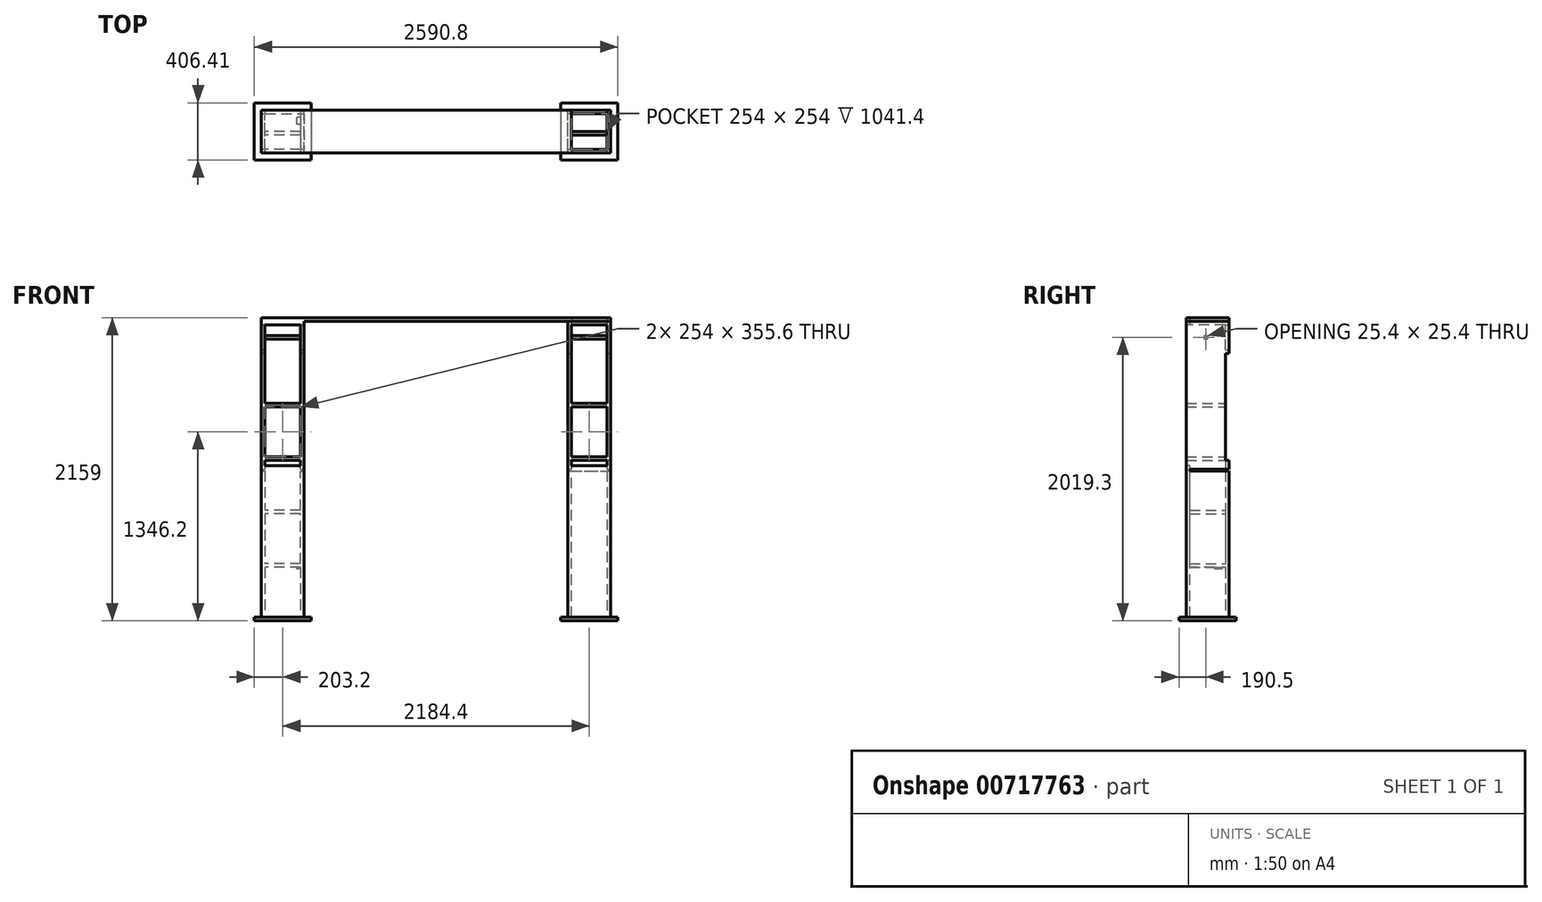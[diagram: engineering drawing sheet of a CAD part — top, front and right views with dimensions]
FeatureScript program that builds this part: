
annotation { "Feature Type Name" : "Feature", "Feature Type Description" : "" }
export const myFeature = defineFeature(function(context is Context, id is Id, definition is map)
    precondition{}
    {
        {
            var Q0;
            Q0=qCreatedBy(makeId("Front.planeOp"),FACE);
            var sketch = newSketch(context, id + "F0", { "sketchPlane" : qUnion([Q0])});
            skLineSegment(sketch, "E0", {"start": v(0, 0) * mm, "end": v(939.8, 0) * mm});
            skLineSegment(sketch, "E1", {"start": v(939.8, 0) * mm, "end": v(939.8, 1066.8) * mm});
            skLineSegment(sketch, "E2", {"start": v(939.8, 1066.8) * mm, "end": v(1244.6, 1066.8) * mm});
            skLineSegment(sketch, "E3", {"start": v(1244.6, 1066.8) * mm, "end": v(1244.6, 0) * mm});
            skLineSegment(sketch, "E4.MirrorCS", {"start": v(0, 0) * mm, "end": v(-939.8, 0) * mm});
            skLineSegment(sketch, "E5.MirrorCS", {"start": v(-939.8, 0) * mm, "end": v(-939.8, 1066.8) * mm});
            skLineSegment(sketch, "E6.MirrorCS", {"start": v(-939.8, 1066.8) * mm, "end": v(-1244.6, 1066.8) * mm});
            skLineSegment(sketch, "E7.MirrorCS", {"start": v(-1244.6, 1066.8) * mm, "end": v(-1244.6, 0) * mm});
            skLineSegment(sketch, "E8.MirrorCS", {"start": v(-939.8, 0) * mm, "end": v(-939.8, -1066.8) * mm});
            skLineSegment(sketch, "E9.MirrorCS", {"start": v(-1244.6, -1066.8) * mm, "end": v(-1244.6, 0) * mm});
            skLineSegment(sketch, "E10.MirrorCS", {"start": v(-939.8, -1066.8) * mm, "end": v(-1244.6, -1066.8) * mm});
            skLineSegment(sketch, "E11.MirrorCS", {"start": v(939.8, 0) * mm, "end": v(939.8, -1066.8) * mm});
            skLineSegment(sketch, "E12.MirrorCS", {"start": v(1244.6, -1066.8) * mm, "end": v(1244.6, 0) * mm});
            skLineSegment(sketch, "E13.MirrorCS", {"start": v(939.8, -1066.8) * mm, "end": v(1244.6, -1066.8) * mm});
            skLineSegment(sketch, "E14", {"start": v(939.8, 0) * mm, "end": v(1244.6, 0) * mm});
            skLineSegment(sketch, "E15", {"start": v(939.8, 0) * mm, "end": v(939.8, 12.7) * mm});
            skLineSegment(sketch, "E16", {"start": v(939.8, 12.7) * mm, "end": v(1244.6, 12.7) * mm});
            skLineSegment(sketch, "E17", {"start": v(1244.6, 12.7) * mm, "end": v(1244.6, 0) * mm});
            skLineSegment(sketch, "E18.MirrorCS", {"start": v(-939.8, 12.7) * mm, "end": v(-1244.6, 12.7) * mm});
            skLineSegment(sketch, "E19.MirrorCS", {"start": v(-939.8, 0) * mm, "end": v(-1244.6, 0) * mm});
            skLineSegment(sketch, "E20", {"start": v(-939.8, 12.7) * mm, "end": v(-939.8, 0) * mm});
            skLineSegment(sketch, "E21", {"start": v(-1244.6, 12.7) * mm, "end": v(-1244.6, 0) * mm});
            skSolve(sketch);
        }
        {
            var Q0;
            Q0=makeQuery(id+"F0.imprint","IMPRINT",FACE,{"disambiguationData":[TD([[makeQuery(id+"F0.imprint","IMPRINT",EDGE,{"derivedFrom":sQuery(id+"F0.wireOp",EDGE,"E1")}),-1.0]])]});
            var Q1;
            Q1=makeQuery(id+"F0.imprint","IMPRINT",FACE,{"disambiguationData":[TD([[makeQuery(id+"F0.imprint","IMPRINT",EDGE,{"derivedFrom":sQuery(id+"F0.wireOp",EDGE,"E11.MirrorCS")}),1.0]])]});
            var Q2;
            Q2=makeQuery(id+"F0.imprint","IMPRINT",FACE,{"disambiguationData":[TD([[makeQuery(id+"F0.imprint","IMPRINT",EDGE,{"derivedFrom":sQuery(id+"F0.wireOp",EDGE,"E5.MirrorCS")}),1.0]])]});
            var Q3;
            Q3=makeQuery(id+"F0.imprint","IMPRINT",FACE,{"disambiguationData":[TD([[makeQuery(id+"F0.imprint","IMPRINT",EDGE,{"derivedFrom":sQuery(id+"F0.wireOp",EDGE,"E8.MirrorCS")}),-1.0]])]});
            extrude(context, id + "F1", {"entities" : qUnion([Q0, Q1, Q2, Q3]), "depth" : 25.4 * mm, "offsetDistance" : 25.4 * mm});
        }
        {
            var Q0;
            Q0=makeQuery(id+"F1.opExtrude","SWEPT_FACE",FACE,{"disambiguationData":[OSD([sQuery(id+"F0.wireOp",EDGE,"E3"),sQuery(id+"F0.wireOp",EDGE,"E12.MirrorCS")])]});
            var sketch = newSketch(context, id + "F2", { "sketchPlane" : qUnion([Q0])});
            skLineSegment(sketch, "E22", {"start": v(0, 1066.8) * mm, "end": v(279.4, 1066.8) * mm});
            skLineSegment(sketch, "E23", {"start": v(0, -1066.8) * mm, "end": v(279.4, -1066.8) * mm});
            skLineSegment(sketch, "E24", {"start": v(279.4, 1066.8) * mm, "end": v(279.4, -1066.8) * mm});
            skLineSegment(sketch, "E25", {"start": v(0, 12.7) * mm, "end": v(279.4, 12.7) * mm});
            skLineSegment(sketch, "E26", {"start": v(0, 0) * mm, "end": v(279.4, 0) * mm});
            skLineSegment(sketch, "E27", {"start": v(279.4, 0) * mm, "end": v(279.4, 12.7) * mm});
            skLineSegment(sketch, "E28", {"start": v(0, 12.7) * mm, "end": v(0, 0) * mm});
            skLineSegment(sketch, "E29", {"start": v(0, 1066.8) * mm, "end": v(2.54, 1066.8) * mm});
            skLineSegment(sketch, "E30", {"start": v(2.54, 1066.8) * mm, "end": v(2.54, -1066.8) * mm});
            skPoint(sketch, "E30.endSnap0", {"position": v(139.7, -1066.8) * mm});
            skLineSegment(sketch, "E31", {"start": v(2.54, -1066.8) * mm, "end": v(0, -1066.8) * mm});
            skSolve(sketch);
        }
        {
            var Q0;
            {var subQ0=sQuery(id+"F2.wireOp",EDGE,"E22");Q0=makeQuery(id+"F2.imprint","IMPRINT",FACE,{"disambiguationData":[TD([[makeQuery(id+"F2.imprint","IMPRINT",EDGE,{"derivedFrom":subQ0}),-1.0]])]});}
            var Q1;
            {var subQ0=sQuery(id+"F2.wireOp",EDGE,"E23");Q1=makeQuery(id+"F2.imprint","IMPRINT",FACE,{"disambiguationData":[TD([[makeQuery(id+"F2.imprint","IMPRINT",EDGE,{"derivedFrom":subQ0}),1.0]])]});}
            extrude(context, id + "F3", {"entities" : qUnion([Q0, Q1]), "oppositeDirection" : true, "depth" : 25.4 * mm, "offsetDistance" : 25.4 * mm});
        }
        {
            var Q0;
            Q0=makeQuery(id+"F3.opExtrude","SWEPT_FACE",FACE,{"disambiguationData":[OSD([sQuery(id+"F2.wireOp",EDGE,"E24")])]});
            var sketch = newSketch(context, id + "F4", { "sketchPlane" : qUnion([Q0])});
            skLineSegment(sketch, "E32", {"start": v(-1219.2, 1066.8) * mm, "end": v(-965.2, 1066.8) * mm});
            skLineSegment(sketch, "E33", {"start": v(-1219.2, -1066.8) * mm, "end": v(-965.2, -1066.8) * mm});
            skLineSegment(sketch, "E34", {"start": v(-965.2, 1066.8) * mm, "end": v(-965.2, -1066.8) * mm});
            skLineSegment(sketch, "E35", {"start": v(-1219.2, 12.7) * mm, "end": v(-965.2, 12.7) * mm});
            skLineSegment(sketch, "E36", {"start": v(-965.2, 12.7) * mm, "end": v(-965.2, 0) * mm});
            skLineSegment(sketch, "E37", {"start": v(-965.2, 0) * mm, "end": v(-1219.2, 0) * mm});
            skLineSegment(sketch, "E38", {"start": v(-1219.2, 0) * mm, "end": v(-1219.2, 12.7) * mm});
            skSolve(sketch);
        }
        {
            var Q0;
            {var subQ0=sQuery(id+"F4.wireOp",EDGE,"E33");Q0=makeQuery(id+"F4.imprint","IMPRINT",FACE,{"disambiguationData":[TD([[makeQuery(id+"F4.imprint","IMPRINT",EDGE,{"derivedFrom":subQ0}),1.0]])]});}
            var Q1;
            {var subQ0=sQuery(id+"F4.wireOp",EDGE,"E32");Q1=makeQuery(id+"F4.imprint","IMPRINT",FACE,{"disambiguationData":[TD([[makeQuery(id+"F4.imprint","IMPRINT",EDGE,{"derivedFrom":subQ0}),-1.0]])]});}
            extrude(context, id + "F5", {"entities" : qUnion([Q0, Q1]), "oppositeDirection" : true, "depth" : 25.4 * mm, "offsetDistance" : 25.4 * mm});
        }
        {
            var Q0;
            Q0=makeQuery(id+"F5.opExtrude","SWEPT_FACE",FACE,{"disambiguationData":[OSD([sQuery(id+"F4.wireOp",EDGE,"E34")])]});
            var sketch = newSketch(context, id + "F6", { "sketchPlane" : qUnion([Q0])});
            skLineSegment(sketch, "E39", {"start": v(-279.4, 1066.8) * mm, "end": v(0, 1066.8) * mm});
            skLineSegment(sketch, "E40", {"start": v(-279.4, -1066.8) * mm, "end": v(0, -1066.8) * mm});
            skLineSegment(sketch, "E41", {"start": v(0, -1066.8) * mm, "end": v(0, 1066.8) * mm});
            skLineSegment(sketch, "E42", {"start": v(-279.4, 1066.8) * mm, "end": v(-279.4, -1066.8) * mm});
            skLineSegment(sketch, "E43", {"start": v(0, 0) * mm, "end": v(0, 12.7) * mm});
            skLineSegment(sketch, "E44", {"start": v(0, 12.7) * mm, "end": v(-279.4, 12.7) * mm});
            skLineSegment(sketch, "E45", {"start": v(-279.4, 12.7) * mm, "end": v(-279.4, 0) * mm});
            skLineSegment(sketch, "E46", {"start": v(-279.4, 0) * mm, "end": v(0, 0) * mm});
            skSolve(sketch);
        }
        {
            var Q0;
            {var subQ2=sQuery(id+"F6.wireOp",EDGE,"E41");Q0=makeQuery(id+"F6.imprint","IMPRINT",FACE,{"disambiguationData":[TD([[makeQuery(id+"F6.imprint","IMPRINT",EDGE,{"derivedFrom":subQ2}),1.0]])]});}
            var Q1;
            {var subQ0=sQuery(id+"F6.wireOp",EDGE,"E42");Q1=makeQuery(id+"F6.imprint","IMPRINT",FACE,{"disambiguationData":[TD([[makeQuery(id+"F6.imprint","IMPRINT",EDGE,{"derivedFrom":subQ0}),1.0]])]});}
            extrude(context, id + "F7", {"entities" : qUnion([Q0, Q1]), "depth" : 25.4 * mm, "offsetDistance" : 25.4 * mm});
        }
        {
            var Q0;
            Q0=makeQuery(id+"F5.opExtrude","SWEPT_BODY",BODY,{"disambiguationData":[OSD([sQuery(id+"F2.wireOp",EDGE,"E24"),sQuery(id+"F4.wireOp",EDGE,"E32"),sQuery(id+"F4.wireOp",EDGE,"E33"),sQuery(id+"F4.wireOp",EDGE,"E34")])]});
            var Q1;
            Q1=makeQuery(id+"F7.opExtrude","SWEPT_BODY",BODY,{"disambiguationData":[OSD([sQuery(id+"F6.wireOp",EDGE,"E39"),sQuery(id+"F6.wireOp",EDGE,"E40"),sQuery(id+"F6.wireOp",EDGE,"E41"),sQuery(id+"F6.wireOp",EDGE,"E42")])]});
            var Q2;
            Q2=makeQuery(id+"F1.opExtrude","SWEPT_BODY",BODY,{"disambiguationData":[OSD([sQuery(id+"F0.wireOp",EDGE,"E1"),sQuery(id+"F0.wireOp",EDGE,"E2"),sQuery(id+"F0.wireOp",EDGE,"E3"),sQuery(id+"F0.wireOp",EDGE,"E11.MirrorCS"),sQuery(id+"F0.wireOp",EDGE,"E12.MirrorCS"),sQuery(id+"F0.wireOp",EDGE,"E13.MirrorCS")])]});
            var Q3;
            Q3=makeQuery(id+"F3.opExtrude","SWEPT_BODY",BODY,{"disambiguationData":[OSD([sQuery(id+"F0.wireOp",EDGE,"E3"),sQuery(id+"F0.wireOp",EDGE,"E12.MirrorCS"),sQuery(id+"F2.wireOp",EDGE,"E22"),sQuery(id+"F2.wireOp",EDGE,"E23"),sQuery(id+"F2.wireOp",EDGE,"E24")])]});
            var Q4;
            Q4=qCreatedBy(makeId("Right.planeOp"),FACE);
            mirror(context, id + "F8", {"operationType" : NewBodyOperationType.ADD, "entities" : qUnion([Q0, Q1, Q2, Q3]), "mirrorPlane" : qUnion([Q4])});
        }
        {
            var Q0;
            Q0=makeQuery(id+"F8.boolean.opBoolean","MERGE",FACE,{"derivedFrom":[makeQuery(id+"F1.opExtrude","SWEPT_FACE",FACE,{"disambiguationData":[OSD([sQuery(id+"F0.wireOp",EDGE,"E13.MirrorCS")])]}),makeQuery(id+"F3.opExtrude","SWEPT_FACE",FACE,{"disambiguationData":[OSD([sQuery(id+"F2.wireOp",EDGE,"E23")])]}),makeQuery(id+"F5.opExtrude","SWEPT_FACE",FACE,{"disambiguationData":[OSD([sQuery(id+"F4.wireOp",EDGE,"E33")])]}),makeQuery(id+"F7.opExtrude","SWEPT_FACE",FACE,{"disambiguationData":[OSD([sQuery(id+"F6.wireOp",EDGE,"E40")])]})]});
            var sketch = newSketch(context, id + "F9", { "sketchPlane" : qUnion([Q0])});
            skLineSegment(sketch, "E47", {"start": v(939.8, 25.4) * mm, "end": v(889, 25.4) * mm});
            skLineSegment(sketch, "E48", {"start": v(939.8, 25.4) * mm, "end": v(939.8, 76.2) * mm});
            skLineSegment(sketch, "E49", {"start": v(1244.6, -279.4) * mm, "end": v(1295.4, -279.4) * mm});
            skLineSegment(sketch, "E50", {"start": v(1244.6, -279.4) * mm, "end": v(1244.6, -330.2) * mm});
            skLineSegment(sketch, "E51", {"start": v(1295.4, -279.4) * mm, "end": v(1295.4, -330.2) * mm});
            skLineSegment(sketch, "E52", {"start": v(1295.4, -330.2) * mm, "end": v(1244.6, -330.2) * mm});
            skLineSegment(sketch, "E53", {"start": v(889, 25.4) * mm, "end": v(889, 76.2) * mm});
            skLineSegment(sketch, "E54", {"start": v(889, 76.2) * mm, "end": v(939.8, 76.2) * mm});
            skLineSegment(sketch, "E55", {"start": v(939.8, 76.2) * mm, "end": v(1295.4, 76.2) * mm});
            skLineSegment(sketch, "E56", {"start": v(1295.4, 76.2) * mm, "end": v(1295.4, -279.4) * mm});
            skLineSegment(sketch, "E57", {"start": v(1244.6, -330.2) * mm, "end": v(889, -330.2) * mm});
            skLineSegment(sketch, "E58", {"start": v(889, -330.2) * mm, "end": v(889, 25.4) * mm});
            skSolve(sketch);
        }
        {
            var Q0;
            Q0=makeQuery(id+"F9.imprint","IMPRINT",FACE,{"disambiguationData":[TD([[makeQuery(id+"F9.imprint","IMPRINT",EDGE,{"derivedFrom":sQuery(id+"F9.wireOp",EDGE,"E47")}),1.0]])]});
            var Q1;
            Q1=makeQuery(id+"F9.imprint","IMPRINT",FACE,{"disambiguationData":[TD([[makeQuery(id+"F9.imprint","IMPRINT",EDGE,{"derivedFrom":sQuery(id+"F9.wireOp",EDGE,"E47")}),-1.0]])]});
            var Q2;
            Q2=makeQuery(id+"F9.imprint","IMPRINT",FACE,{"disambiguationData":[TD([[makeQuery(id+"F9.imprint","IMPRINT",EDGE,{"derivedFrom":sQuery(id+"F9.wireOp",EDGE,"E48")}),-1.0]])]});
            var Q3;
            Q3=makeQuery(id+"F9.imprint","IMPRINT",FACE,{"disambiguationData":[TD([[makeQuery(id+"F9.imprint","IMPRINT",EDGE,{"derivedFrom":sQuery(id+"F9.wireOp",EDGE,"E49")}),-1.0]])]});
            extrude(context, id + "F10", {"entities" : qUnion([Q0, Q1, Q2, Q3]), "oppositeDirection" : true, "depth" : 25.4 * mm, "offsetDistance" : 25.4 * mm});
        }
        {
            var Q0;
            Q0=makeQuery(id+"F10.opExtrude","SWEPT_BODY",BODY,{"disambiguationData":[OSD([sQuery(id+"F0.wireOp",EDGE,"E11.MirrorCS"),sQuery(id+"F0.wireOp",EDGE,"E12.MirrorCS"),sQuery(id+"F0.wireOp",EDGE,"E13.MirrorCS"),sQuery(id+"F2.wireOp",EDGE,"E23"),sQuery(id+"F2.wireOp",EDGE,"E24"),sQuery(id+"F4.wireOp",EDGE,"E33"),sQuery(id+"F6.wireOp",EDGE,"E40"),sQuery(id+"F6.wireOp",EDGE,"E42"),sQuery(id+"F9.wireOp",EDGE,"E51"),sQuery(id+"F9.wireOp",EDGE,"E52"),sQuery(id+"F9.wireOp",EDGE,"E53"),sQuery(id+"F9.wireOp",EDGE,"E54"),sQuery(id+"F9.wireOp",EDGE,"E55"),sQuery(id+"F9.wireOp",EDGE,"E56"),sQuery(id+"F9.wireOp",EDGE,"E57"),sQuery(id+"F9.wireOp",EDGE,"E58")])]});
            var Q1;
            Q1=qCreatedBy(makeId("Right.planeOp"),FACE);
            mirror(context, id + "F11", {"operationType" : NewBodyOperationType.ADD, "entities" : qUnion([Q0]), "mirrorPlane" : qUnion([Q1])});
        }
        {
            var Q0;
            Q0=makeQuery(id+"F8.boolean.opBoolean","MERGE",FACE,{"derivedFrom":[makeQuery(id+"F1.opExtrude","SWEPT_FACE",FACE,{"disambiguationData":[OSD([sQuery(id+"F0.wireOp",EDGE,"E2")])]}),makeQuery(id+"F3.opExtrude","SWEPT_FACE",FACE,{"disambiguationData":[OSD([sQuery(id+"F2.wireOp",EDGE,"E22")])]}),makeQuery(id+"F5.opExtrude","SWEPT_FACE",FACE,{"disambiguationData":[OSD([sQuery(id+"F4.wireOp",EDGE,"E32")])]}),makeQuery(id+"F7.opExtrude","SWEPT_FACE",FACE,{"disambiguationData":[OSD([sQuery(id+"F6.wireOp",EDGE,"E39")])]})]});
            var sketch = newSketch(context, id + "F12", { "sketchPlane" : qUnion([Q0])});
            skLineSegment(sketch, "E59", {"start": v(1244.6, 279.4) * mm, "end": v(-1244.6, 279.4) * mm});
            skLineSegment(sketch, "E60", {"start": v(-1244.6, 279.4) * mm, "end": v(-1244.6, -25.4) * mm});
            skLineSegment(sketch, "E61.MirrorCS", {"start": v(1244.6, 279.4) * mm, "end": v(1244.6, -25.4) * mm});
            skLineSegment(sketch, "E62", {"start": v(-1244.6, -25.4) * mm, "end": v(1244.6, -25.4) * mm});
            skLineSegment(sketch, "E63", {"start": v(939.8, 279.4) * mm, "end": v(939.8, -25.4) * mm});
            skSolve(sketch);
        }
        {
            var Q0;
            {var subQ2=sQuery(id+"F12.wireOp",EDGE,"E60");Q0=makeQuery(id+"F12.imprint","IMPRINT",FACE,{"disambiguationData":[TD([[makeQuery(id+"F12.imprint","IMPRINT",EDGE,{"derivedFrom":subQ2}),1.0]])]});}
            var Q1;
            {var subQ2=sQuery(id+"F12.wireOp",EDGE,"E61.MirrorCS");Q1=makeQuery(id+"F12.imprint","IMPRINT",FACE,{"disambiguationData":[TD([[makeQuery(id+"F12.imprint","IMPRINT",EDGE,{"derivedFrom":subQ2}),1.0]])]});}
            var Q2;
            Q2=makeQuery(id+"F12.imprint","IMPRINT",FACE,{"disambiguationData":[TD([[makeQuery(id+"F12.imprint","IMPRINT",EDGE,{"derivedFrom":makeQuery(id+"F5.opExtrude","CAP_EDGE",EDGE,{"disambiguationData":[OSD([sQuery(id+"F4.wireOp",EDGE,"E32")])],"isStart":false})}),1.0]])]});
            var Q3;
            Q3=sQuery(id+"F12.wireOp",EDGE,"E63");
            var Q4;
            Q4=sQuery(id+"F12.wireOp",EDGE,"E62");
            var Q5;
            Q5=sQuery(id+"F12.wireOp",EDGE,"E61.MirrorCS");
            var Q6;
            Q6=sQuery(id+"F12.wireOp",EDGE,"E59");
            extrude(context, id + "F13", {"entities" : qUnion([Q0, Q1, Q2]), "surfaceOperationType" : NewSurfaceOperationType.ADD, "surfaceEntities" : qUnion([Q3, Q4, Q5, Q6]), "depth" : 25.4 * mm, "offsetDistance" : 25.4 * mm});
        }
        {
            var Q0;
            Q0=makeQuery(id+"F1.opExtrude","CAP_FACE",FACE,{"disambiguationData":[OSD([sQuery(id+"F0.wireOp",EDGE,"E1"),sQuery(id+"F0.wireOp",EDGE,"E2"),sQuery(id+"F0.wireOp",EDGE,"E3"),sQuery(id+"F0.wireOp",EDGE,"E11.MirrorCS"),sQuery(id+"F0.wireOp",EDGE,"E12.MirrorCS"),sQuery(id+"F0.wireOp",EDGE,"E13.MirrorCS")])],"isStart":false});
            var sketch = newSketch(context, id + "F14", { "sketchPlane" : qUnion([Q0])});
            skLineSegment(sketch, "E64", {"start": v(939.8, 1066.8) * mm, "end": v(965.2, 1066.8) * mm});
            skLineSegment(sketch, "E65", {"start": v(939.8, 1066.8) * mm, "end": v(939.8, 1041.4) * mm});
            skLineSegment(sketch, "E66", {"start": v(965.2, 1066.8) * mm, "end": v(965.2, -1041.4) * mm});
            skLineSegment(sketch, "E67", {"start": v(965.2, -1041.4) * mm, "end": v(965.2, -1016) * mm});
            skLineSegment(sketch, "E68", {"start": v(1244.6, -1016) * mm, "end": v(939.8, -1016) * mm});
            skLineSegment(sketch, "E69", {"start": v(1244.6, -1041.4) * mm, "end": v(939.8, -1041.4) * mm});
            skLineSegment(sketch, "E70", {"start": v(939.8, -1041.4) * mm, "end": v(939.8, 1066.8) * mm});
            skLineSegment(sketch, "E71", {"start": v(1244.6, -1016) * mm, "end": v(1219.2, -1016) * mm});
            skLineSegment(sketch, "E72", {"start": v(1219.2, -1041.4) * mm, "end": v(1219.2, 1066.8) * mm});
            skLineSegment(sketch, "E73", {"start": v(939.8, 1041.4) * mm, "end": v(1244.6, 1041.4) * mm});
            skLineSegment(sketch, "E74", {"start": v(965.2, -1016) * mm, "end": v(965.2, 12.7) * mm});
            skLineSegment(sketch, "E75", {"start": v(965.2, 12.7) * mm, "end": v(1219.2, 12.7) * mm});
            skLineSegment(sketch, "E76", {"start": v(965.2, 12.7) * mm, "end": v(965.2, 25.4) * mm});
            skLineSegment(sketch, "E77", {"start": v(965.2, 12.7) * mm, "end": v(965.2, 0) * mm});
            skLineSegment(sketch, "E78", {"start": v(1219.2, 12.7) * mm, "end": v(1219.2, 25.4) * mm});
            skLineSegment(sketch, "E79", {"start": v(1219.2, 12.7) * mm, "end": v(1219.2, 0) * mm});
            skLineSegment(sketch, "E80", {"start": v(965.2, 25.4) * mm, "end": v(1219.2, 25.4) * mm});
            skLineSegment(sketch, "E81", {"start": v(965.2, 0) * mm, "end": v(1219.2, 0) * mm});
            skLineSegment(sketch, "E82.MirrorCS", {"start": v(-965.2, 1066.8) * mm, "end": v(-965.2, -1041.4) * mm});
            skLineSegment(sketch, "E83.MirrorCS", {"start": v(-1219.2, -1041.4) * mm, "end": v(-1219.2, 1066.8) * mm});
            skLineSegment(sketch, "E84.MirrorCS", {"start": v(-1244.6, -1016) * mm, "end": v(-939.8, -1016) * mm});
            skLineSegment(sketch, "E85.MirrorCS", {"start": v(-939.8, 1041.4) * mm, "end": v(-1244.6, 1041.4) * mm});
            skLineSegment(sketch, "E86", {"start": v(-1219.2, 0) * mm, "end": v(-1219.2, 12.7) * mm});
            skLineSegment(sketch, "E87", {"start": v(-1219.2, 12.7) * mm, "end": v(-965.2, 12.7) * mm});
            skLineSegment(sketch, "E88", {"start": v(-965.2, 12.7) * mm, "end": v(-965.2, -12.7) * mm});
            skLineSegment(sketch, "E89", {"start": v(-1219.2, 12.7) * mm, "end": v(-1219.2, -12.7) * mm});
            skLineSegment(sketch, "E90.MirrorCS", {"start": v(-965.2, 12.7) * mm, "end": v(-965.2, 38.1) * mm});
            skLineSegment(sketch, "E91", {"start": v(-1219.2, 12.7) * mm, "end": v(-1219.2, 38.1) * mm});
            skLineSegment(sketch, "E92", {"start": v(-965.2, 38.1) * mm, "end": v(-1219.2, 38.1) * mm});
            skLineSegment(sketch, "E93", {"start": v(-965.2, -12.7) * mm, "end": v(-1219.2, -12.7) * mm});
            skLineSegment(sketch, "E94.MirrorCS", {"start": v(965.2, 38.1) * mm, "end": v(1219.2, 38.1) * mm});
            skLineSegment(sketch, "E95.MirrorCS", {"start": v(1219.2, 12.7) * mm, "end": v(965.2, 12.7) * mm});
            skLineSegment(sketch, "E96.MirrorCS", {"start": v(965.2, -12.7) * mm, "end": v(1219.2, -12.7) * mm});
            skSolve(sketch);
        }
        {
            var Q0;
            {var subQ0=sQuery(id+"F14.wireOp",EDGE,"E92");Q0=makeQuery(id+"F14.imprint","IMPRINT",FACE,{"disambiguationData":[TD([[makeQuery(id+"F14.imprint","IMPRINT",EDGE,{"derivedFrom":subQ0}),-1.0]])]});}
            var Q1;
            {var subQ0=sQuery(id+"F14.wireOp",EDGE,"E94.MirrorCS");Q1=makeQuery(id+"F14.imprint","IMPRINT",FACE,{"disambiguationData":[TD([[makeQuery(id+"F14.imprint","IMPRINT",EDGE,{"derivedFrom":subQ0}),1.0]])]});}
            extrude(context, id + "F15", {"entities" : qUnion([Q0, Q1]), "operationType" : NewBodyOperationType.REMOVE, "oppositeDirection" : true, "depth" : 25.4 * mm, "offsetDistance" : 25.4 * mm});
        }
        {
            var Q0;
            {var subQ0=sQuery(id+"F2.wireOp",EDGE,"E24");Q0=makeQuery(id+"F8.boolean.opBoolean","MERGE",FACE,{"derivedFrom":[makeQuery(id+"F3.opExtrude","SWEPT_FACE",FACE,{"disambiguationData":[OSD([subQ0])]}),makeQuery(id+"F5.opExtrude","CAP_FACE",FACE,{"disambiguationData":[OSD([subQ0,sQuery(id+"F4.wireOp",EDGE,"E32"),sQuery(id+"F4.wireOp",EDGE,"E33"),sQuery(id+"F4.wireOp",EDGE,"E34")])],"isStart":true}),makeQuery(id+"F7.opExtrude","SWEPT_FACE",FACE,{"disambiguationData":[OSD([sQuery(id+"F6.wireOp",EDGE,"E42")])]})]});}
            var sketch = newSketch(context, id + "F16", { "sketchPlane" : qUnion([Q0])});
            skLineSegment(sketch, "E97", {"start": v(-1244.6, 1066.8) * mm, "end": v(-1244.6, -1041.4) * mm});
            skLineSegment(sketch, "E98", {"start": v(-1244.6, -1041.4) * mm, "end": v(-1244.6, 1066.8) * mm});
            skLineSegment(sketch, "E99", {"start": v(-1244.6, -1041.4) * mm, "end": v(-1244.6, -685.8) * mm});
            skLineSegment(sketch, "E100", {"start": v(-1244.6, -685.8) * mm, "end": v(-1244.6, -660.4) * mm});
            skLineSegment(sketch, "E101", {"start": v(-1244.6, -660.4) * mm, "end": v(-1244.6, -304.8) * mm});
            skLineSegment(sketch, "E102", {"start": v(-1244.6, -304.8) * mm, "end": v(-1244.6, -279.4) * mm});
            skLineSegment(sketch, "E103", {"start": v(-1244.6, -279.4) * mm, "end": v(-1244.6, 76.2) * mm});
            skLineSegment(sketch, "E104", {"start": v(-1244.6, 76.2) * mm, "end": v(-1244.6, 101.6) * mm});
            skLineSegment(sketch, "E105", {"start": v(-1244.6, 101.6) * mm, "end": v(-1244.6, 457.2) * mm});
            skLineSegment(sketch, "E106", {"start": v(-1244.6, 457.2) * mm, "end": v(-1244.6, 482.6) * mm});
            skLineSegment(sketch, "E107", {"start": v(-1244.6, 482.6) * mm, "end": v(-1244.6, 838.2) * mm});
            skLineSegment(sketch, "E108", {"start": v(-1244.6, 539.75) * mm, "end": v(-1244.6, 838.2) * mm});
            skLineSegment(sketch, "E109", {"start": v(-1244.6, 838.2) * mm, "end": v(-1244.6, 863.6) * mm});
            skLineSegment(sketch, "E110", {"start": v(-1244.6, 863.6) * mm, "end": v(-1244.6, 1041.4) * mm});
            skLineSegment(sketch, "E111", {"start": v(-1244.6, 1041.4) * mm, "end": v(-1244.6, 1066.8) * mm});
            skLineSegment(sketch, "E112", {"start": v(-939.8, 1066.8) * mm, "end": v(-1244.6, 1066.8) * mm});
            skLineSegment(sketch, "E113", {"start": v(-939.8, 1041.4) * mm, "end": v(-939.8, 539.75) * mm});
            skLineSegment(sketch, "E114", {"start": v(-1244.6, 863.6) * mm, "end": v(-939.8, 863.6) * mm});
            skLineSegment(sketch, "E115", {"start": v(-939.8, 863.6) * mm, "end": v(-939.8, 838.2) * mm});
            skLineSegment(sketch, "E116", {"start": v(-939.8, 838.2) * mm, "end": v(-1244.6, 838.2) * mm});
            skLineSegment(sketch, "E117", {"start": v(-1244.6, 482.6) * mm, "end": v(-939.8, 482.6) * mm});
            skLineSegment(sketch, "E118", {"start": v(-939.8, 482.6) * mm, "end": v(-939.8, 838.2) * mm});
            skLineSegment(sketch, "E119", {"start": v(-1244.6, 457.2) * mm, "end": v(-939.8, 457.2) * mm});
            skLineSegment(sketch, "E120", {"start": v(-939.8, 457.2) * mm, "end": v(-939.8, 482.6) * mm});
            skLineSegment(sketch, "E121", {"start": v(-939.8, 838.2) * mm, "end": v(-939.8, 482.6) * mm});
            skLineSegment(sketch, "E122", {"start": v(-1244.6, 101.6) * mm, "end": v(-939.8, 101.6) * mm});
            skLineSegment(sketch, "E123", {"start": v(-939.8, 101.6) * mm, "end": v(-939.8, 457.2) * mm});
            skLineSegment(sketch, "E124", {"start": v(-1244.6, 76.2) * mm, "end": v(-939.8, 76.2) * mm});
            skLineSegment(sketch, "E125", {"start": v(-939.8, 76.2) * mm, "end": v(-939.8, 101.6) * mm});
            skLineSegment(sketch, "E126", {"start": v(-1244.6, -279.4) * mm, "end": v(-939.8, -279.4) * mm});
            skLineSegment(sketch, "E127", {"start": v(-939.8, -279.4) * mm, "end": v(-939.8, 76.2) * mm});
            skLineSegment(sketch, "E128", {"start": v(-1244.6, -304.8) * mm, "end": v(-939.8, -304.8) * mm});
            skLineSegment(sketch, "E129", {"start": v(-939.8, -304.8) * mm, "end": v(-939.8, -279.4) * mm});
            skLineSegment(sketch, "E130", {"start": v(-1244.6, -660.4) * mm, "end": v(-939.8, -660.4) * mm});
            skLineSegment(sketch, "E131", {"start": v(-939.8, -660.4) * mm, "end": v(-939.8, -304.8) * mm});
            skLineSegment(sketch, "E132", {"start": v(-1244.6, -685.8) * mm, "end": v(-939.8, -685.8) * mm});
            skLineSegment(sketch, "E133", {"start": v(-939.8, -685.8) * mm, "end": v(-939.8, -1041.4) * mm});
            skLineSegment(sketch, "E134", {"start": v(-939.8, -1041.4) * mm, "end": v(-1244.6, -1041.4) * mm});
            skLineSegment(sketch, "E135.MirrorCS", {"start": v(1244.6, -1041.4) * mm, "end": v(1244.6, 1066.8) * mm});
            skLineSegment(sketch, "E136.MirrorCS", {"start": v(1244.6, 482.6) * mm, "end": v(939.8, 482.6) * mm});
            skLineSegment(sketch, "E137.MirrorCS", {"start": v(1244.6, 457.2) * mm, "end": v(939.8, 457.2) * mm});
            skLineSegment(sketch, "E138.MirrorCS", {"start": v(1244.6, 101.6) * mm, "end": v(939.8, 101.6) * mm});
            skLineSegment(sketch, "E139.MirrorCS", {"start": v(1244.6, 76.2) * mm, "end": v(939.8, 76.2) * mm});
            skLineSegment(sketch, "E140.MirrorCS", {"start": v(1244.6, -279.4) * mm, "end": v(939.8, -279.4) * mm});
            skLineSegment(sketch, "E141.MirrorCS", {"start": v(1244.6, -304.8) * mm, "end": v(939.8, -304.8) * mm});
            skLineSegment(sketch, "E142.MirrorCS", {"start": v(1244.6, -660.4) * mm, "end": v(939.8, -660.4) * mm});
            skLineSegment(sketch, "E143.MirrorCS", {"start": v(1244.6, -685.8) * mm, "end": v(939.8, -685.8) * mm});
            skLineSegment(sketch, "E144.MirrorCS", {"start": v(1244.6, -279.4) * mm, "end": v(1244.6, 76.2) * mm});
            skLineSegment(sketch, "E145.MirrorCS", {"start": v(1244.6, -660.4) * mm, "end": v(1244.6, -304.8) * mm});
            skLineSegment(sketch, "E146.MirrorCS", {"start": v(1244.6, -1041.4) * mm, "end": v(1244.6, -685.8) * mm});
            skLineSegment(sketch, "E147.MirrorCS", {"start": v(1244.6, 101.6) * mm, "end": v(1244.6, 457.2) * mm});
            skLineSegment(sketch, "E148.MirrorCS", {"start": v(939.8, 1041.4) * mm, "end": v(939.8, 539.75) * mm});
            skLineSegment(sketch, "E149.MirrorCS", {"start": v(939.8, 482.6) * mm, "end": v(939.8, 838.2) * mm});
            skLineSegment(sketch, "E150.MirrorCS", {"start": v(939.8, 101.6) * mm, "end": v(939.8, 457.2) * mm});
            skLineSegment(sketch, "E151.MirrorCS", {"start": v(939.8, -279.4) * mm, "end": v(939.8, 76.2) * mm});
            skLineSegment(sketch, "E152.MirrorCS", {"start": v(939.8, -660.4) * mm, "end": v(939.8, -304.8) * mm});
            skLineSegment(sketch, "E153.MirrorCS", {"start": v(939.8, -685.8) * mm, "end": v(939.8, -1041.4) * mm});
            skLineSegment(sketch, "E154.MirrorCS", {"start": v(939.8, 863.6) * mm, "end": v(939.8, 838.2) * mm});
            skLineSegment(sketch, "E155", {"start": v(939.8, 838.2) * mm, "end": v(1244.6, 838.2) * mm});
            skLineSegment(sketch, "E156", {"start": v(1244.6, 838.2) * mm, "end": v(1244.6, 863.6) * mm});
            skLineSegment(sketch, "E157", {"start": v(1244.6, 863.6) * mm, "end": v(939.8, 863.6) * mm});
            skLineSegment(sketch, "E158", {"start": v(939.8, 1041.4) * mm, "end": v(1244.6, 1041.4) * mm});
            skLineSegment(sketch, "E159", {"start": v(1244.6, 1041.4) * mm, "end": v(1244.6, 1066.8) * mm});
            skLineSegment(sketch, "E160", {"start": v(1244.6, 1066.8) * mm, "end": v(939.8, 1066.8) * mm});
            skLineSegment(sketch, "E161", {"start": v(939.8, 1066.8) * mm, "end": v(939.8, 1041.4) * mm});
            skLineSegment(sketch, "E162", {"start": v(939.8, 1041.4) * mm, "end": v(939.8, 863.6) * mm});
            skLineSegment(sketch, "E163", {"start": v(939.8, -304.8) * mm, "end": v(939.8, -279.4) * mm});
            skLineSegment(sketch, "E164", {"start": v(939.8, 76.2) * mm, "end": v(939.8, 101.6) * mm});
            skLineSegment(sketch, "E165", {"start": v(939.8, 457.2) * mm, "end": v(939.8, 482.6) * mm});
            skLineSegment(sketch, "E166", {"start": v(939.8, -660.4) * mm, "end": v(939.8, -685.8) * mm});
            skLineSegment(sketch, "E167", {"start": v(939.8, -1041.4) * mm, "end": v(1244.6, -1041.4) * mm});
            skLineSegment(sketch, "E168", {"start": v(939.8, 1066.8) * mm, "end": v(1244.6, 1066.8) * mm});
            skSolve(sketch);
        }
        {
            var Q0;
            Q0=makeQuery(id+"F16.imprint","IMPRINT",FACE,{"disambiguationData":[TD([[makeQuery(id+"F16.imprint","IMPRINT",EDGE,{"derivedFrom":sQuery(id+"F16.wireOp",EDGE,"E99")}),1.0]])]});
            var Q1;
            Q1=makeQuery(id+"F16.imprint","IMPRINT",FACE,{"disambiguationData":[TD([[makeQuery(id+"F16.imprint","IMPRINT",EDGE,{"derivedFrom":sQuery(id+"F16.wireOp",EDGE,"E101")}),1.0]])]});
            var Q2;
            Q2=makeQuery(id+"F16.imprint","IMPRINT",FACE,{"disambiguationData":[TD([[makeQuery(id+"F16.imprint","IMPRINT",EDGE,{"derivedFrom":sQuery(id+"F16.wireOp",EDGE,"E103")}),1.0]])]});
            var Q3;
            Q3=makeQuery(id+"F16.imprint","IMPRINT",FACE,{"disambiguationData":[TD([[makeQuery(id+"F16.imprint","IMPRINT",EDGE,{"derivedFrom":sQuery(id+"F16.wireOp",EDGE,"E105")}),1.0]])]});
            var Q4;
            Q4=makeQuery(id+"F16.imprint","IMPRINT",FACE,{"disambiguationData":[TD([[makeQuery(id+"F16.imprint","IMPRINT",EDGE,{"derivedFrom":sQuery(id+"F16.wireOp",EDGE,"E107")}),1.0]])]});
            var Q5;
            {var subQ1=sQuery(id+"F16.wireOp",EDGE,"ooY9xAKW-JCIj-mzVf-GkQX-W2rqI5djVSOr");Q5=makeQuery(id+"F16.imprint","IMPRINT",FACE,{"disambiguationData":[TD([[makeQuery(id+"F16.imprint","IMPRINT",EDGE,{"derivedFrom":subQ1}),-1.0]])]});}
            var Q6;
            Q6=makeQuery(id+"F16.imprint","IMPRINT",FACE,{"disambiguationData":[TD([[makeQuery(id+"F16.imprint","IMPRINT",EDGE,{"derivedFrom":sQuery(id+"F16.wireOp",EDGE,"rzhm8GGH-gWjN-RGGv-JU4R-XMMNJH5SbDe0")}),1.0]])]});
            var Q7;
            Q7=makeQuery(id+"F16.imprint","IMPRINT",FACE,{"disambiguationData":[TD([[makeQuery(id+"F16.imprint","IMPRINT",EDGE,{"derivedFrom":sQuery(id+"F16.wireOp",EDGE,"RmI45enO-YM0h-No7n-si8y-LCqarBK098rO")}),1.0]])]});
            var Q8;
            Q8=makeQuery(id+"F16.imprint","IMPRINT",FACE,{"disambiguationData":[TD([[makeQuery(id+"F16.imprint","IMPRINT",EDGE,{"derivedFrom":sQuery(id+"F16.wireOp",EDGE,"pSO2kT9N-3fWK-h8cs-pWX5-nwyGKKmIl5mG")}),1.0]])]});
            var Q9;
            Q9=makeQuery(id+"F16.imprint","IMPRINT",FACE,{"disambiguationData":[TD([[makeQuery(id+"F16.imprint","IMPRINT",EDGE,{"derivedFrom":sQuery(id+"F16.wireOp",EDGE,"E98")}),1.0]])]});
            var Q10;
            {var subQ0=sQuery(id+"F16.wireOp",EDGE,"7c41313c-4230-4134-9dff-f753b0ed85a40.MirrorCS");Q10=makeQuery(id+"F16.imprint","IMPRINT",FACE,{"disambiguationData":[TD([[makeQuery(id+"F16.imprint","IMPRINT",EDGE,{"derivedFrom":subQ0}),-1.0]])]});}
            var Q11;
            {var subQ0=sQuery(id+"F16.wireOp",EDGE,"08005356-4b95-4076-bdfd-29439a82fed30.MirrorCS");Q11=makeQuery(id+"F16.imprint","IMPRINT",FACE,{"disambiguationData":[TD([[makeQuery(id+"F16.imprint","IMPRINT",EDGE,{"derivedFrom":subQ0}),-1.0]])]});}
            var Q12;
            Q12=makeQuery(id+"F16.imprint","IMPRINT",FACE,{"disambiguationData":[TD([[makeQuery(id+"F16.imprint","IMPRINT",EDGE,{"derivedFrom":sQuery(id+"F16.wireOp",EDGE,"5705823b-c1d4-4691-b0c9-69c018d08e420.MirrorCS")}),1.0]])]});
            var Q13;
            {var subQ3=sQuery(id+"F16.wireOp",EDGE,"E157");Q13=makeQuery(id+"F16.imprint","IMPRINT",FACE,{"disambiguationData":[TD([[makeQuery(id+"F16.imprint","IMPRINT",EDGE,{"derivedFrom":subQ3}),-1.0]])]});}
            var Q14;
            {var subQ0=sQuery(id+"F16.wireOp",EDGE,"E136.MirrorCS");Q14=makeQuery(id+"F16.imprint","IMPRINT",FACE,{"disambiguationData":[TD([[makeQuery(id+"F16.imprint","IMPRINT",EDGE,{"derivedFrom":subQ0}),-1.0]])]});}
            var Q15;
            {var subQ0=sQuery(id+"F16.wireOp",EDGE,"E137.MirrorCS");Q15=makeQuery(id+"F16.imprint","IMPRINT",FACE,{"disambiguationData":[TD([[makeQuery(id+"F16.imprint","IMPRINT",EDGE,{"derivedFrom":subQ0}),1.0]])]});}
            var Q16;
            {var subQ0=sQuery(id+"F16.wireOp",EDGE,"E139.MirrorCS");Q16=makeQuery(id+"F16.imprint","IMPRINT",FACE,{"disambiguationData":[TD([[makeQuery(id+"F16.imprint","IMPRINT",EDGE,{"derivedFrom":subQ0}),1.0]])]});}
            var Q17;
            {var subQ0=sQuery(id+"F16.wireOp",EDGE,"E141.MirrorCS");Q17=makeQuery(id+"F16.imprint","IMPRINT",FACE,{"disambiguationData":[TD([[makeQuery(id+"F16.imprint","IMPRINT",EDGE,{"derivedFrom":subQ0}),1.0]])]});}
            var Q18;
            {var subQ0=sQuery(id+"F16.wireOp",EDGE,"E143.MirrorCS");Q18=makeQuery(id+"F16.imprint","IMPRINT",FACE,{"disambiguationData":[TD([[makeQuery(id+"F16.imprint","IMPRINT",EDGE,{"derivedFrom":subQ0}),1.0]])]});}
            var Q19;
            {var subQ0=sQuery(id+"F16.wireOp",EDGE,"7298b8d0-efe0-44e3-b066-829b78df03ea0.MirrorCS");Q19=makeQuery(id+"F16.imprint","IMPRINT",FACE,{"disambiguationData":[TD([[makeQuery(id+"F16.imprint","IMPRINT",EDGE,{"derivedFrom":subQ0}),1.0]])]});}
            var Q20;
            {var subQ0=sQuery(id+"F16.wireOp",EDGE,"E122");Q20=makeQuery(id+"F16.imprint","IMPRINT",FACE,{"disambiguationData":[TD([[makeQuery(id+"F16.imprint","IMPRINT",EDGE,{"derivedFrom":subQ0}),-1.0]])]});}
            var Q21;
            Q21=makeQuery(id+"F16.imprint","IMPRINT",FACE,{"disambiguationData":[TD([[makeQuery(id+"F16.imprint","IMPRINT",EDGE,{"derivedFrom":sQuery(id+"F16.wireOp",EDGE,"E102")}),1.0]])]});
            var Q22;
            Q22=makeQuery(id+"F16.imprint","IMPRINT",FACE,{"disambiguationData":[TD([[makeQuery(id+"F16.imprint","IMPRINT",EDGE,{"derivedFrom":sQuery(id+"F16.wireOp",EDGE,"E100")}),1.0]])]});
            var Q23;
            {var subQ0=sQuery(id+"F16.wireOp",EDGE,"E142.MirrorCS");Q23=makeQuery(id+"F16.imprint","IMPRINT",FACE,{"disambiguationData":[TD([[makeQuery(id+"F16.imprint","IMPRINT",EDGE,{"derivedFrom":subQ0}),1.0]])]});}
            var Q24;
            {var subQ0=sQuery(id+"F16.wireOp",EDGE,"E140.MirrorCS");Q24=makeQuery(id+"F16.imprint","IMPRINT",FACE,{"disambiguationData":[TD([[makeQuery(id+"F16.imprint","IMPRINT",EDGE,{"derivedFrom":subQ0}),1.0]])]});}
            var Q25;
            {var subQ0=sQuery(id+"F16.wireOp",EDGE,"E138.MirrorCS");Q25=makeQuery(id+"F16.imprint","IMPRINT",FACE,{"disambiguationData":[TD([[makeQuery(id+"F16.imprint","IMPRINT",EDGE,{"derivedFrom":subQ0}),1.0]])]});}
            var Q26;
            {var subQ0=sQuery(id+"F16.wireOp",EDGE,"E136.MirrorCS");Q26=makeQuery(id+"F16.imprint","IMPRINT",FACE,{"disambiguationData":[TD([[makeQuery(id+"F16.imprint","IMPRINT",EDGE,{"derivedFrom":subQ0}),1.0]])]});}
            var Q27;
            Q27=makeQuery(id+"F16.imprint","IMPRINT",FACE,{"disambiguationData":[TD([[makeQuery(id+"F16.imprint","IMPRINT",EDGE,{"derivedFrom":sQuery(id+"F16.wireOp",EDGE,"E154.MirrorCS")}),1.0]])]});
            var Q28;
            Q28=makeQuery(id+"F16.imprint","IMPRINT",FACE,{"disambiguationData":[TD([[makeQuery(id+"F16.imprint","IMPRINT",EDGE,{"derivedFrom":sQuery(id+"F16.wireOp",EDGE,"E158")}),1.0]])]});
            var Q29;
            {var subQ0=sQuery(id+"F16.wireOp",EDGE,"E117");Q29=makeQuery(id+"F16.imprint","IMPRINT",FACE,{"disambiguationData":[TD([[makeQuery(id+"F16.imprint","IMPRINT",EDGE,{"derivedFrom":subQ0}),-1.0]])]});}
            var Q30;
            Q30=makeQuery(id+"F16.imprint","IMPRINT",FACE,{"disambiguationData":[TD([[makeQuery(id+"F16.imprint","IMPRINT",EDGE,{"derivedFrom":sQuery(id+"F16.wireOp",EDGE,"E109")}),1.0]])]});
            var Q31;
            {var subQ0=sQuery(id+"F16.wireOp",EDGE,"E116");Q31=makeQuery(id+"F16.imprint","IMPRINT",FACE,{"disambiguationData":[TD([[makeQuery(id+"F16.imprint","IMPRINT",EDGE,{"derivedFrom":subQ0}),1.0]])]});}
            var Q32;
            Q32=makeQuery(id+"F16.imprint","IMPRINT",FACE,{"disambiguationData":[TD([[makeQuery(id+"F16.imprint","IMPRINT",EDGE,{"derivedFrom":sQuery(id+"F16.wireOp",EDGE,"E110")}),1.0]])]});
            var Q33;
            {var subQ0=sQuery(id+"F16.wireOp",EDGE,"E119");Q33=makeQuery(id+"F16.imprint","IMPRINT",FACE,{"disambiguationData":[TD([[makeQuery(id+"F16.imprint","IMPRINT",EDGE,{"derivedFrom":subQ0}),-1.0]])]});}
            extrude(context, id + "F17", {"entities" : qUnion([Q0, Q1, Q2, Q3, Q4, Q5, Q6, Q7, Q8, Q9, Q10, Q11, Q12, Q13, Q14, Q15, Q16, Q17, Q18, Q19, Q20, Q21, Q22, Q23, Q24, Q25, Q26, Q27, Q28, Q29, Q30, Q31, Q32, Q33]), "operationType" : NewBodyOperationType.REMOVE, "oppositeDirection" : true, "depth" : 25.4 * mm, "offsetDistance" : 25.4 * mm});
        }
        {
            var Q0;
            Q0=makeQuery(id+"F16.imprint","IMPRINT",FACE,{"disambiguationData":[TD([[makeQuery(id+"F16.imprint","IMPRINT",EDGE,{"derivedFrom":sQuery(id+"F16.wireOp",EDGE,"uJaQ9J3y-J2yZ-1Nu6-E8s8-Kf6XV3nzCr8D")}),1.0]])]});
            var Q1;
            Q1=makeQuery(id+"F16.imprint","IMPRINT",FACE,{"disambiguationData":[TD([[makeQuery(id+"F16.imprint","IMPRINT",EDGE,{"derivedFrom":sQuery(id+"F16.wireOp",EDGE,"y7MJIetr-xdzX-xa1W-oi4v-hxO5LGBLeZjA")}),1.0]])]});
            var Q2;
            Q2=makeQuery(id+"F16.imprint","IMPRINT",FACE,{"disambiguationData":[TD([[makeQuery(id+"F16.imprint","IMPRINT",EDGE,{"derivedFrom":sQuery(id+"F16.wireOp",EDGE,"gtivugSo-fAOk-aDXs-cSH7-A13Mfpiq2l9o")}),1.0]])]});
            var Q3;
            Q3=makeQuery(id+"F16.imprint","IMPRINT",FACE,{"disambiguationData":[TD([[makeQuery(id+"F16.imprint","IMPRINT",EDGE,{"derivedFrom":sQuery(id+"F16.wireOp",EDGE,"E106")}),1.0]])]});
            var Q4;
            Q4=makeQuery(id+"F16.imprint","IMPRINT",FACE,{"disambiguationData":[TD([[makeQuery(id+"F16.imprint","IMPRINT",EDGE,{"derivedFrom":sQuery(id+"F16.wireOp",EDGE,"E104")}),1.0]])]});
            var Q5;
            Q5=makeQuery(id+"F16.imprint","IMPRINT",FACE,{"disambiguationData":[TD([[makeQuery(id+"F16.imprint","IMPRINT",EDGE,{"derivedFrom":sQuery(id+"F16.wireOp",EDGE,"E102")}),1.0]])]});
            var Q6;
            Q6=makeQuery(id+"F16.imprint","IMPRINT",FACE,{"disambiguationData":[TD([[makeQuery(id+"F16.imprint","IMPRINT",EDGE,{"derivedFrom":sQuery(id+"F16.wireOp",EDGE,"E100")}),1.0]])]});
            var Q7;
            {var subQ0=sQuery(id+"F16.wireOp",EDGE,"7c41313c-4230-4134-9dff-f753b0ed85a40.MirrorCS");Q7=makeQuery(id+"F16.imprint","IMPRINT",FACE,{"disambiguationData":[TD([[makeQuery(id+"F16.imprint","IMPRINT",EDGE,{"derivedFrom":subQ0}),1.0]])]});}
            var Q8;
            {var subQ0=sQuery(id+"F16.wireOp",EDGE,"e39053fc-3253-493d-8556-e0671f5e092e0.MirrorCS");Q8=makeQuery(id+"F16.imprint","IMPRINT",FACE,{"disambiguationData":[TD([[makeQuery(id+"F16.imprint","IMPRINT",EDGE,{"derivedFrom":subQ0}),1.0]])]});}
            var Q9;
            {var subQ0=sQuery(id+"F16.wireOp",EDGE,"7WP0m2Jd-dBDp-E99x-Hb5a-TRlt7vfgwMC8");Q9=makeQuery(id+"F16.imprint","IMPRINT",FACE,{"disambiguationData":[TD([[makeQuery(id+"F16.imprint","IMPRINT",EDGE,{"derivedFrom":subQ0}),-1.0]])]});}
            var Q10;
            Q10=makeQuery(id+"F16.imprint","IMPRINT",FACE,{"disambiguationData":[TD([[makeQuery(id+"F16.imprint","IMPRINT",EDGE,{"derivedFrom":sQuery(id+"F16.wireOp",EDGE,"E158")}),1.0]])]});
            var Q11;
            {var subQ0=sQuery(id+"F16.wireOp",EDGE,"E136.MirrorCS");Q11=makeQuery(id+"F16.imprint","IMPRINT",FACE,{"disambiguationData":[TD([[makeQuery(id+"F16.imprint","IMPRINT",EDGE,{"derivedFrom":subQ0}),1.0]])]});}
            var Q12;
            {var subQ0=sQuery(id+"F16.wireOp",EDGE,"E138.MirrorCS");Q12=makeQuery(id+"F16.imprint","IMPRINT",FACE,{"disambiguationData":[TD([[makeQuery(id+"F16.imprint","IMPRINT",EDGE,{"derivedFrom":subQ0}),1.0]])]});}
            var Q13;
            {var subQ0=sQuery(id+"F16.wireOp",EDGE,"E140.MirrorCS");Q13=makeQuery(id+"F16.imprint","IMPRINT",FACE,{"disambiguationData":[TD([[makeQuery(id+"F16.imprint","IMPRINT",EDGE,{"derivedFrom":subQ0}),1.0]])]});}
            var Q14;
            {var subQ0=sQuery(id+"F16.wireOp",EDGE,"E142.MirrorCS");Q14=makeQuery(id+"F16.imprint","IMPRINT",FACE,{"disambiguationData":[TD([[makeQuery(id+"F16.imprint","IMPRINT",EDGE,{"derivedFrom":subQ0}),1.0]])]});}
            var Q15;
            {var subQ0=sQuery(id+"F16.wireOp",EDGE,"E122");Q15=makeQuery(id+"F16.imprint","IMPRINT",FACE,{"disambiguationData":[TD([[makeQuery(id+"F16.imprint","IMPRINT",EDGE,{"derivedFrom":subQ0}),-1.0]])]});}
            var Q16;
            {var subQ0=sQuery(id+"F16.wireOp",EDGE,"E117");Q16=makeQuery(id+"F16.imprint","IMPRINT",FACE,{"disambiguationData":[TD([[makeQuery(id+"F16.imprint","IMPRINT",EDGE,{"derivedFrom":subQ0}),-1.0]])]});}
            extrude(context, id + "F18", {"entities" : qUnion([Q0, Q1, Q2, Q3, Q4, Q5, Q6, Q7, Q8, Q9, Q10, Q11, Q12, Q13, Q14, Q15, Q16]), "operationType" : NewBodyOperationType.ADD, "oppositeDirection" : true, "depth" : 304.8 * mm, "offsetDistance" : 25.4 * mm});
        }
        {
            var Q0;
            Q0=makeQuery(id+"F8.boolean.opBoolean","MERGE",FACE,{"derivedFrom":[makeQuery(id+"F1.opExtrude","SWEPT_FACE",FACE,{"disambiguationData":[OSD([sQuery(id+"F0.wireOp",EDGE,"E13.MirrorCS")])]}),makeQuery(id+"F3.opExtrude","SWEPT_FACE",FACE,{"disambiguationData":[OSD([sQuery(id+"F2.wireOp",EDGE,"E23")])]}),makeQuery(id+"F5.opExtrude","SWEPT_FACE",FACE,{"disambiguationData":[OSD([sQuery(id+"F4.wireOp",EDGE,"E33")])]}),makeQuery(id+"F7.opExtrude","SWEPT_FACE",FACE,{"disambiguationData":[OSD([sQuery(id+"F6.wireOp",EDGE,"E40")])]})]});
            var sketch = newSketch(context, id + "F19", { "sketchPlane" : qUnion([Q0])});
            skLineSegment(sketch, "E169", {"start": v(1219.2, 0) * mm, "end": v(965.2, 0) * mm});
            skLineSegment(sketch, "E170", {"start": v(965.2, 0) * mm, "end": v(965.2, -254) * mm});
            skLineSegment(sketch, "E171", {"start": v(965.2, -254) * mm, "end": v(1219.2, -254) * mm});
            skLineSegment(sketch, "E172", {"start": v(1219.2, -254) * mm, "end": v(1219.2, 0) * mm});
            skSolve(sketch);
        }
        {
            var Q0;
            Q0=makeQuery(id+"F19.imprint","IMPRINT",FACE,{"disambiguationData":[TD([[makeQuery(id+"F19.imprint","IMPRINT",EDGE,{"derivedFrom":sQuery(id+"F19.wireOp",EDGE,"E169")}),-1.0]])]});
            extrude(context, id + "F20", {"entities" : qUnion([Q0]), "oppositeDirection" : true, "depth" : 25.4 * mm, "offsetDistance" : 25.4 * mm});
        }
        {
            var Q0;
            Q0=makeQuery(id+"F20.opExtrude","SWEPT_BODY",BODY,{"disambiguationData":[OSD([sQuery(id+"F19.wireOp",EDGE,"E169"),sQuery(id+"F19.wireOp",EDGE,"E170"),sQuery(id+"F19.wireOp",EDGE,"E171"),sQuery(id+"F19.wireOp",EDGE,"E172")])]});
            var Q1;
            Q1=qCreatedBy(makeId("Right.planeOp"),FACE);
            mirror(context, id + "F21", {"operationType" : NewBodyOperationType.ADD, "entities" : qUnion([Q0]), "mirrorPlane" : qUnion([Q1])});
        }
        {
            var Q0;
            Q0=makeQuery(id+"F16.imprint","IMPRINT",FACE,{"disambiguationData":[TD([[makeQuery(id+"F16.imprint","IMPRINT",EDGE,{"derivedFrom":sQuery(id+"F16.wireOp",EDGE,"E109")}),1.0]])]});
            var Q1;
            {var subQ0=sQuery(id+"F16.wireOp",EDGE,"E117");Q1=makeQuery(id+"F16.imprint","IMPRINT",FACE,{"disambiguationData":[TD([[makeQuery(id+"F16.imprint","IMPRINT",EDGE,{"derivedFrom":subQ0}),-1.0]])]});}
            var Q2;
            {var subQ0=sQuery(id+"F16.wireOp",EDGE,"E122");Q2=makeQuery(id+"F16.imprint","IMPRINT",FACE,{"disambiguationData":[TD([[makeQuery(id+"F16.imprint","IMPRINT",EDGE,{"derivedFrom":subQ0}),-1.0]])]});}
            var Q3;
            Q3=makeQuery(id+"F16.imprint","IMPRINT",FACE,{"disambiguationData":[TD([[makeQuery(id+"F16.imprint","IMPRINT",EDGE,{"derivedFrom":sQuery(id+"F16.wireOp",EDGE,"E102")}),1.0]])]});
            var Q4;
            Q4=makeQuery(id+"F16.imprint","IMPRINT",FACE,{"disambiguationData":[TD([[makeQuery(id+"F16.imprint","IMPRINT",EDGE,{"derivedFrom":sQuery(id+"F16.wireOp",EDGE,"E100")}),1.0]])]});
            var Q5;
            {var subQ0=sQuery(id+"F16.wireOp",EDGE,"E142.MirrorCS");Q5=makeQuery(id+"F16.imprint","IMPRINT",FACE,{"disambiguationData":[TD([[makeQuery(id+"F16.imprint","IMPRINT",EDGE,{"derivedFrom":subQ0}),1.0]])]});}
            var Q6;
            {var subQ0=sQuery(id+"F16.wireOp",EDGE,"E140.MirrorCS");Q6=makeQuery(id+"F16.imprint","IMPRINT",FACE,{"disambiguationData":[TD([[makeQuery(id+"F16.imprint","IMPRINT",EDGE,{"derivedFrom":subQ0}),1.0]])]});}
            var Q7;
            {var subQ0=sQuery(id+"F16.wireOp",EDGE,"E138.MirrorCS");Q7=makeQuery(id+"F16.imprint","IMPRINT",FACE,{"disambiguationData":[TD([[makeQuery(id+"F16.imprint","IMPRINT",EDGE,{"derivedFrom":subQ0}),1.0]])]});}
            var Q8;
            {var subQ0=sQuery(id+"F16.wireOp",EDGE,"E136.MirrorCS");Q8=makeQuery(id+"F16.imprint","IMPRINT",FACE,{"disambiguationData":[TD([[makeQuery(id+"F16.imprint","IMPRINT",EDGE,{"derivedFrom":subQ0}),1.0]])]});}
            var Q9;
            Q9=makeQuery(id+"F16.imprint","IMPRINT",FACE,{"disambiguationData":[TD([[makeQuery(id+"F16.imprint","IMPRINT",EDGE,{"derivedFrom":sQuery(id+"F16.wireOp",EDGE,"E154.MirrorCS")}),1.0]])]});
            extrude(context, id + "F22", {"entities" : qUnion([Q0, Q1, Q2, Q3, Q4, Q5, Q6, Q7, Q8, Q9]), "operationType" : NewBodyOperationType.REMOVE, "oppositeDirection" : true, "depth" : 25.4 * mm, "offsetDistance" : 25.4 * mm});
        }
        {
            var Q0;
            Q0=makeQuery(id+"F18.opExtrude","SWEPT_FACE",FACE,{"disambiguationData":[OSD([sQuery(id+"F16.wireOp",EDGE,"E143.MirrorCS")])]});
            var sketch = newSketch(context, id + "F23", { "sketchPlane" : qUnion([Q0])});
            skLineSegment(sketch, "E173", {"start": v(-939.8, -254) * mm, "end": v(-939.8, -228.6) * mm});
            skLineSegment(sketch, "E174", {"start": v(-939.8, -228.6) * mm, "end": v(-965.2, -228.6) * mm});
            skLineSegment(sketch, "E175", {"start": v(-965.2, -228.6) * mm, "end": v(-965.2, -177.8) * mm});
            skLineSegment(sketch, "E176", {"start": v(-965.2, -177.8) * mm, "end": v(-939.8, -177.8) * mm});
            skLineSegment(sketch, "E177", {"start": v(-939.8, -177.8) * mm, "end": v(-939.8, -228.6) * mm});
            skLineSegment(sketch, "E178", {"start": v(-939.8, -254) * mm, "end": v(-1092.2, -254) * mm});
            skLineSegment(sketch, "E179", {"start": v(-1092.2, -254) * mm, "end": v(-1244.6, -254) * mm});
            skLineSegment(sketch, "E180", {"start": v(-1244.6, -254) * mm, "end": v(-1244.6, -228.6) * mm});
            skLineSegment(sketch, "E181", {"start": v(-1092.2, -254) * mm, "end": v(-1092.2, -115.79) * mm});
            skLineSegment(sketch, "E182.MirrorCS", {"start": v(-1219.2, -228.6) * mm, "end": v(-1219.2, -177.8) * mm});
            skLineSegment(sketch, "E183.MirrorCS", {"start": v(-1244.6, -177.8) * mm, "end": v(-1244.6, -228.6) * mm});
            skLineSegment(sketch, "E184.MirrorCS", {"start": v(-1219.2, -177.8) * mm, "end": v(-1244.6, -177.8) * mm});
            skLineSegment(sketch, "E185.MirrorCS", {"start": v(-1244.6, -228.6) * mm, "end": v(-1219.2, -228.6) * mm});
            skLineSegment(sketch, "E186", {"start": v(-1219.2, -177.8) * mm, "end": v(-1193.8, -177.8) * mm});
            skLineSegment(sketch, "E187", {"start": v(-1219.2, -228.6) * mm, "end": v(-1193.8, -228.6) * mm});
            skLineSegment(sketch, "E188", {"start": v(-1193.8, -177.8) * mm, "end": v(-1193.8, -228.6) * mm});
            skLineSegment(sketch, "E189.MirrorCS", {"start": v(-965.2, -177.8) * mm, "end": v(-990.6, -177.8) * mm});
            skLineSegment(sketch, "E190.MirrorCS", {"start": v(-990.6, -177.8) * mm, "end": v(-990.6, -228.6) * mm});
            skLineSegment(sketch, "E191.MirrorCS", {"start": v(-965.2, -228.6) * mm, "end": v(-990.6, -228.6) * mm});
            skSolve(sketch);
        }
        {
            var Q0;
            Q0=makeQuery(id+"F23.imprint","IMPRINT",FACE,{"disambiguationData":[TD([[makeQuery(id+"F23.imprint","IMPRINT",EDGE,{"derivedFrom":sQuery(id+"F23.wireOp",EDGE,"E182.MirrorCS")}),-1.0]])]});
            var Q1;
            Q1=makeQuery(id+"F23.imprint","IMPRINT",FACE,{"disambiguationData":[TD([[makeQuery(id+"F23.imprint","IMPRINT",EDGE,{"derivedFrom":sQuery(id+"F23.wireOp",EDGE,"E175")}),1.0]])]});
            extrude(context, id + "F24", {"entities" : qUnion([Q0, Q1]), "operationType" : NewBodyOperationType.ADD, "depth" : 12.7 * mm, "offsetDistance" : 25.4 * mm});
        }
        {
            var Q0;
            {var subQ0=sQuery(id+"F16.wireOp",EDGE,"E108");var subQ1=sQuery(id+"F0.wireOp",EDGE,"E12.MirrorCS");var subQ2=sQuery(id+"F0.wireOp",EDGE,"E3");Q0=makeQuery(id+"F18.boolean.opBoolean","MERGE",FACE,{"derivedFrom":[makeQuery(id+"F8.boolean.opBoolean","MERGE",FACE,{"derivedFrom":[makeQuery(id+"F1.opExtrude","SWEPT_FACE",FACE,{"disambiguationData":[OSD([subQ2,subQ1])]}),makeQuery(id+"F3.opExtrude","CAP_FACE",FACE,{"disambiguationData":[OSD([subQ2,subQ1,sQuery(id+"F2.wireOp",EDGE,"E22"),sQuery(id+"F2.wireOp",EDGE,"E23"),sQuery(id+"F2.wireOp",EDGE,"E24")])],"isStart":true})]}),makeQuery(id+"F18.opExtrude","SWEPT_FACE",FACE,{"disambiguationData":[OSD([sQuery(id+"F16.wireOp",EDGE,"E100")])]}),makeQuery(id+"F18.opExtrude","SWEPT_FACE",FACE,{"disambiguationData":[OSD([sQuery(id+"F16.wireOp",EDGE,"E102")])]}),makeQuery(id+"F18.opExtrude","SWEPT_FACE",FACE,{"disambiguationData":[OSD([subQ0]),TDD([makeQuery(id+"F16.imprint","IMPRINT",EDGE,{"disambiguationData":[TD([[makeQuery(id+"F16.imprint","INTERSECT",VERTEX,{"derivedFrom":[subQ0,sQuery(id+"F16.wireOp",EDGE,"E117")]}),-1.0]])],"derivedFrom":subQ0})])]}),makeQuery(id+"F18.opExtrude","SWEPT_FACE",FACE,{"disambiguationData":[OSD([subQ0]),TDD([makeQuery(id+"F16.imprint","IMPRINT",EDGE,{"disambiguationData":[TD([[makeQuery(id+"F16.imprint","INTERSECT",VERTEX,{"derivedFrom":[subQ0,sQuery(id+"F16.wireOp",EDGE,"E122")]}),-1.0]])],"derivedFrom":subQ0})])]})]});}
            var sketch = newSketch(context, id + "F25", { "sketchPlane" : qUnion([Q0])});
            skLineSegment(sketch, "E192", {"start": v(-25.4, 1066.8) * mm, "end": v(114.3, 1066.8) * mm});
            skLineSegment(sketch, "E193", {"start": v(114.3, 1066.8) * mm, "end": v(114.3, 965.2) * mm});
            skCircle(sketch, "E194", {"center": v(114.3, 952.5) * mm, "radius": 12.7 * mm});
            skLineSegment(sketch, "E195", {"start": v(114.3, 965.2) * mm, "end": v(114.3, 952.5) * mm});
            skLineSegment(sketch, "E196.MirrorCS", {"start": v(-114.3, 1066.8) * mm, "end": v(-114.3, 965.2) * mm});
            skSolve(sketch);
        }
        {
            var Q0;
            Q0=makeQuery(id+"F25.imprint","IMPRINT",FACE,{"disambiguationData":[TD([[makeQuery(id+"F25.imprint","IMPRINT",EDGE,{"derivedFrom":sQuery(id+"F25.wireOp",EDGE,"E194")}),1.0]])]});
            extrude(context, id + "F26", {"entities" : qUnion([Q0]), "operationType" : NewBodyOperationType.ADD, "oppositeDirection" : true, "depth" : 304.8 * mm, "offsetDistance" : 25.4 * mm});
        }
        {
            var Q0;
            {var subQ0=sQuery(id+"F0.wireOp",EDGE,"E12.MirrorCS");var subQ1=sQuery(id+"F0.wireOp",EDGE,"E3");Q0=makeQuery(id+"F8.boolean.opBoolean","MERGE",FACE,{"derivedFrom":[makeQuery(id+"F1.opExtrude","SWEPT_FACE",FACE,{"disambiguationData":[OSD([sQuery(id+"F0.wireOp",EDGE,"E7.MirrorCS"),sQuery(id+"F0.wireOp",EDGE,"E9.MirrorCS")])]}),makeQuery(id+"F8.opPattern","COPY",FACE,{"derivedFrom":makeQuery(id+"F1.opExtrude","SWEPT_FACE",FACE,{"disambiguationData":[OSD([subQ1,subQ0])]}),"instanceName":"1"}),makeQuery(id+"F8.opPattern","COPY",FACE,{"derivedFrom":makeQuery(id+"F3.opExtrude","CAP_FACE",FACE,{"disambiguationData":[OSD([subQ1,subQ0,sQuery(id+"F2.wireOp",EDGE,"E22"),sQuery(id+"F2.wireOp",EDGE,"E23"),sQuery(id+"F2.wireOp",EDGE,"E24")])],"isStart":true}),"instanceName":"1"})]});}
            var sketch = newSketch(context, id + "F27", { "sketchPlane" : qUnion([Q0])});
            skLineSegment(sketch, "E197", {"start": v(-254, 1066.8) * mm, "end": v(-114.3, 1066.8) * mm});
            skLineSegment(sketch, "E198", {"start": v(-114.3, 1066.8) * mm, "end": v(-114.3, 965.2) * mm});
            skLineSegment(sketch, "E199", {"start": v(-114.3, 965.2) * mm, "end": v(-114.3, 952.5) * mm});
            skCircle(sketch, "E200", {"center": v(-114.3, 952.5) * mm, "radius": 12.7 * mm});
            skSolve(sketch);
        }
        {
            var Q0;
            Q0 = qSketchRegion(id + "F27", true);
            extrude(context, id + "F28", {"entities" : qUnion([Q0]), "operationType" : NewBodyOperationType.ADD, "oppositeDirection" : true, "depth" : 304.8 * mm, "offsetDistance" : 25.4 * mm});
        }
        {
            var Q0;
            {var subQ0=sQuery(id+"F16.wireOp",EDGE,"E108");var subQ1=sQuery(id+"F0.wireOp",EDGE,"E12.MirrorCS");var subQ2=sQuery(id+"F0.wireOp",EDGE,"E3");Q0=makeQuery(id+"F18.boolean.opBoolean","MERGE",FACE,{"derivedFrom":[makeQuery(id+"F8.boolean.opBoolean","MERGE",FACE,{"derivedFrom":[makeQuery(id+"F1.opExtrude","SWEPT_FACE",FACE,{"disambiguationData":[OSD([subQ2,subQ1])]}),makeQuery(id+"F3.opExtrude","CAP_FACE",FACE,{"disambiguationData":[OSD([subQ2,subQ1,sQuery(id+"F2.wireOp",EDGE,"E22"),sQuery(id+"F2.wireOp",EDGE,"E23"),sQuery(id+"F2.wireOp",EDGE,"E24")])],"isStart":true})]}),makeQuery(id+"F18.opExtrude","SWEPT_FACE",FACE,{"disambiguationData":[OSD([sQuery(id+"F16.wireOp",EDGE,"E100")])]}),makeQuery(id+"F18.opExtrude","SWEPT_FACE",FACE,{"disambiguationData":[OSD([sQuery(id+"F16.wireOp",EDGE,"E102")])]}),makeQuery(id+"F18.opExtrude","SWEPT_FACE",FACE,{"disambiguationData":[OSD([subQ0]),TDD([makeQuery(id+"F16.imprint","IMPRINT",EDGE,{"disambiguationData":[TD([[makeQuery(id+"F16.imprint","INTERSECT",VERTEX,{"derivedFrom":[subQ0,sQuery(id+"F16.wireOp",EDGE,"E117")]}),-1.0]])],"derivedFrom":subQ0})])]}),makeQuery(id+"F18.opExtrude","SWEPT_FACE",FACE,{"disambiguationData":[OSD([subQ0]),TDD([makeQuery(id+"F16.imprint","IMPRINT",EDGE,{"disambiguationData":[TD([[makeQuery(id+"F16.imprint","INTERSECT",VERTEX,{"derivedFrom":[subQ0,sQuery(id+"F16.wireOp",EDGE,"E122")]}),-1.0]])],"derivedFrom":subQ0})])]})]});}
            var sketch = newSketch(context, id + "F29", { "sketchPlane" : qUnion([Q0])});
            skLineSegment(sketch, "E201", {"start": v(-25.4, 1066.8) * mm, "end": v(0, 1066.8) * mm});
            skLineSegment(sketch, "E202", {"start": v(0, 1066.8) * mm, "end": v(0, -1066.8) * mm});
            skLineSegment(sketch, "E203", {"start": v(0, -1066.8) * mm, "end": v(-25.4, -1066.8) * mm});
            skLineSegment(sketch, "E204", {"start": v(-25.4, -1066.8) * mm, "end": v(-25.4, 1066.8) * mm});
            skSolve(sketch);
        }
        {
            var Q0;
            Q0=sQuery(id+"F29.wireOp",EDGE,"E202");
            extrude(context, id + "F30", {"bodyType" : ToolBodyType.SURFACE, "operationType" : NewBodyOperationType.REMOVE, "surfaceEntities" : qUnion([Q0]), "oppositeDirection" : true, "depth" : 25.4 * mm, "offsetDistance" : 25.4 * mm});
        }
    });
